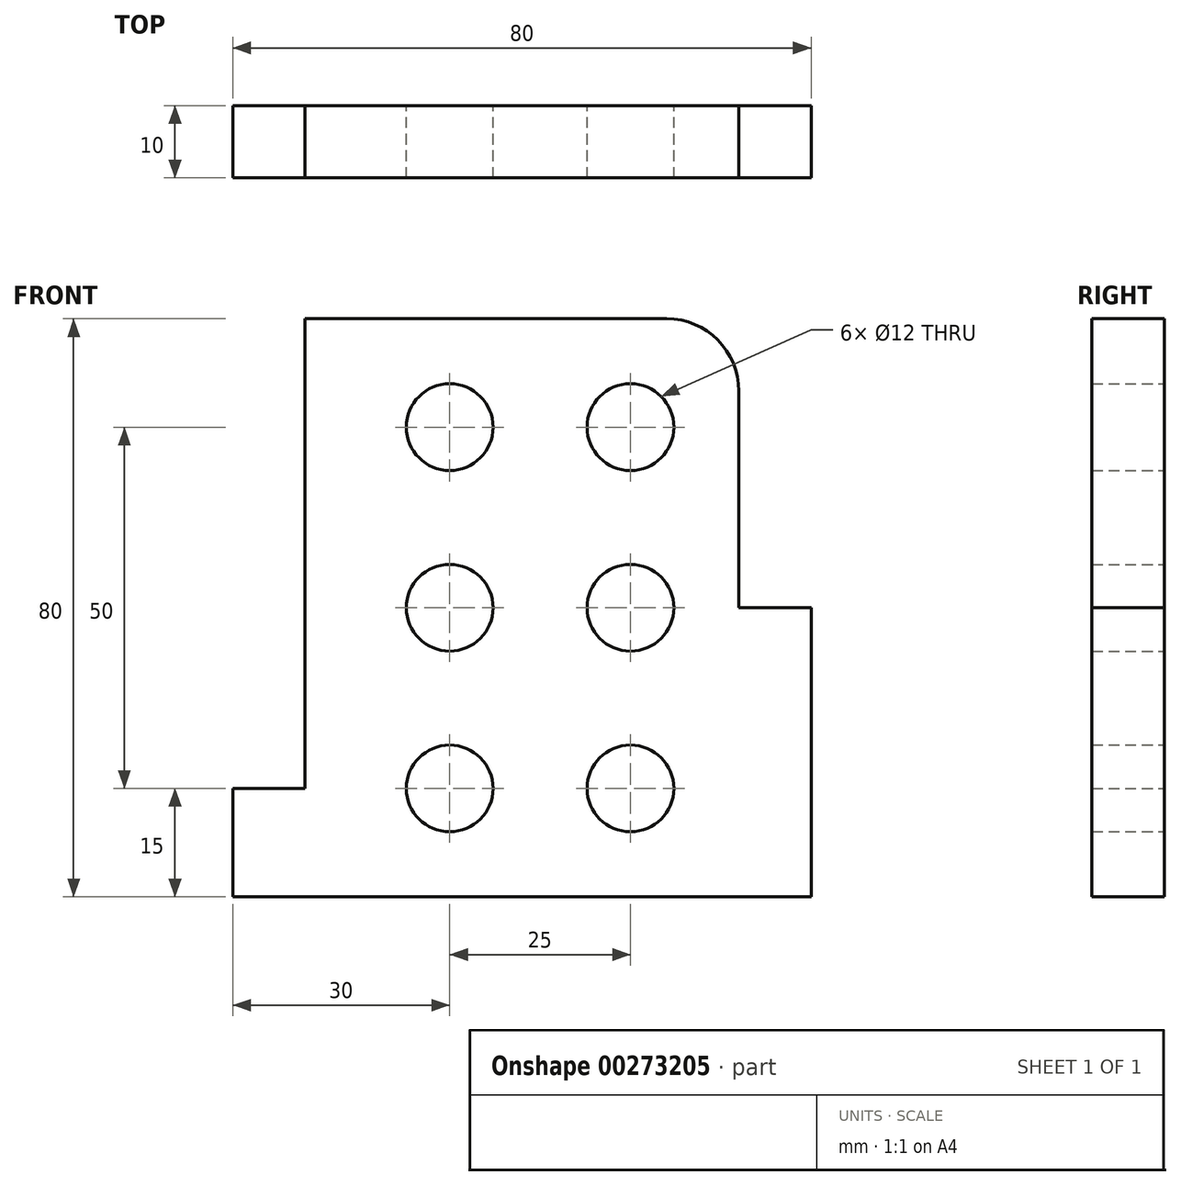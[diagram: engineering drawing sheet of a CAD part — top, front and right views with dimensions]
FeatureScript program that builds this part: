
annotation { "Feature Type Name" : "Feature", "Feature Type Description" : "" }
export const myFeature = defineFeature(function(context is Context, id is Id, definition is map)
    precondition{}
    {
        {
            var Q0;
            Q0=qCreatedBy(makeId("Front.planeOp"),FACE);
            var sketch = newSketch(context, id + "F0", { "sketchPlane" : qUnion([Q0])});
            skLineSegment(sketch, "E0", {"start": v(0, 0) * mm, "end": v(0, 15) * mm});
            skLineSegment(sketch, "E1", {"start": v(0, 15) * mm, "end": v(10, 15) * mm});
            skLineSegment(sketch, "E2", {"start": v(10, 15) * mm, "end": v(10, 80) * mm});
            skLineSegment(sketch, "E3", {"start": v(10, 80) * mm, "end": v(60, 80) * mm});
            skLineSegment(sketch, "E4", {"start": v(0, 0) * mm, "end": v(80, 0) * mm});
            skLineSegment(sketch, "E5", {"start": v(80, 0) * mm, "end": v(80, 40) * mm});
            skLineSegment(sketch, "E6", {"start": v(80, 40) * mm, "end": v(70, 40) * mm});
            skLineSegment(sketch, "E7", {"start": v(70, 40) * mm, "end": v(70, 70) * mm});
            skArc(sketch, "E8", {"start": v(70, 70) * mm, "mid": v(67.07, 77.07) * mm, "end": v(60, 80) * mm});
            skLineSegment(sketch, "E9.bottom", {"start": v(30, 65) * mm, "end": v(55, 65) * mm, "construction": true});
            skLineSegment(sketch, "E9.top", {"start": v(30, 15) * mm, "end": v(55, 15) * mm, "construction": true});
            skLineSegment(sketch, "E9.left", {"start": v(30, 65) * mm, "end": v(30, 15) * mm, "construction": true});
            skLineSegment(sketch, "E9.right", {"start": v(55, 65) * mm, "end": v(55, 15) * mm, "construction": true});
            skLineSegment(sketch, "E10", {"start": v(55, 40) * mm, "end": v(30, 40) * mm, "construction": true});
            skCircle(sketch, "E11", {"center": v(55, 40) * mm, "radius": 6 * mm});
            skCircle(sketch, "E12", {"center": v(55, 65) * mm, "radius": 6 * mm});
            skCircle(sketch, "E13", {"center": v(30, 65) * mm, "radius": 6 * mm});
            skCircle(sketch, "E14", {"center": v(30, 40) * mm, "radius": 6 * mm});
            skCircle(sketch, "E15", {"center": v(30, 15) * mm, "radius": 6 * mm});
            skCircle(sketch, "E16", {"center": v(55, 15) * mm, "radius": 6 * mm});
            skSolve(sketch);
        }
        {
            var Q0;
            Q0 = qSketchRegion(id + "F0", true);
            extrude(context, id + "F1", {"entities" : qUnion([Q0]), "depth" : 10 * mm});
        }
    });
